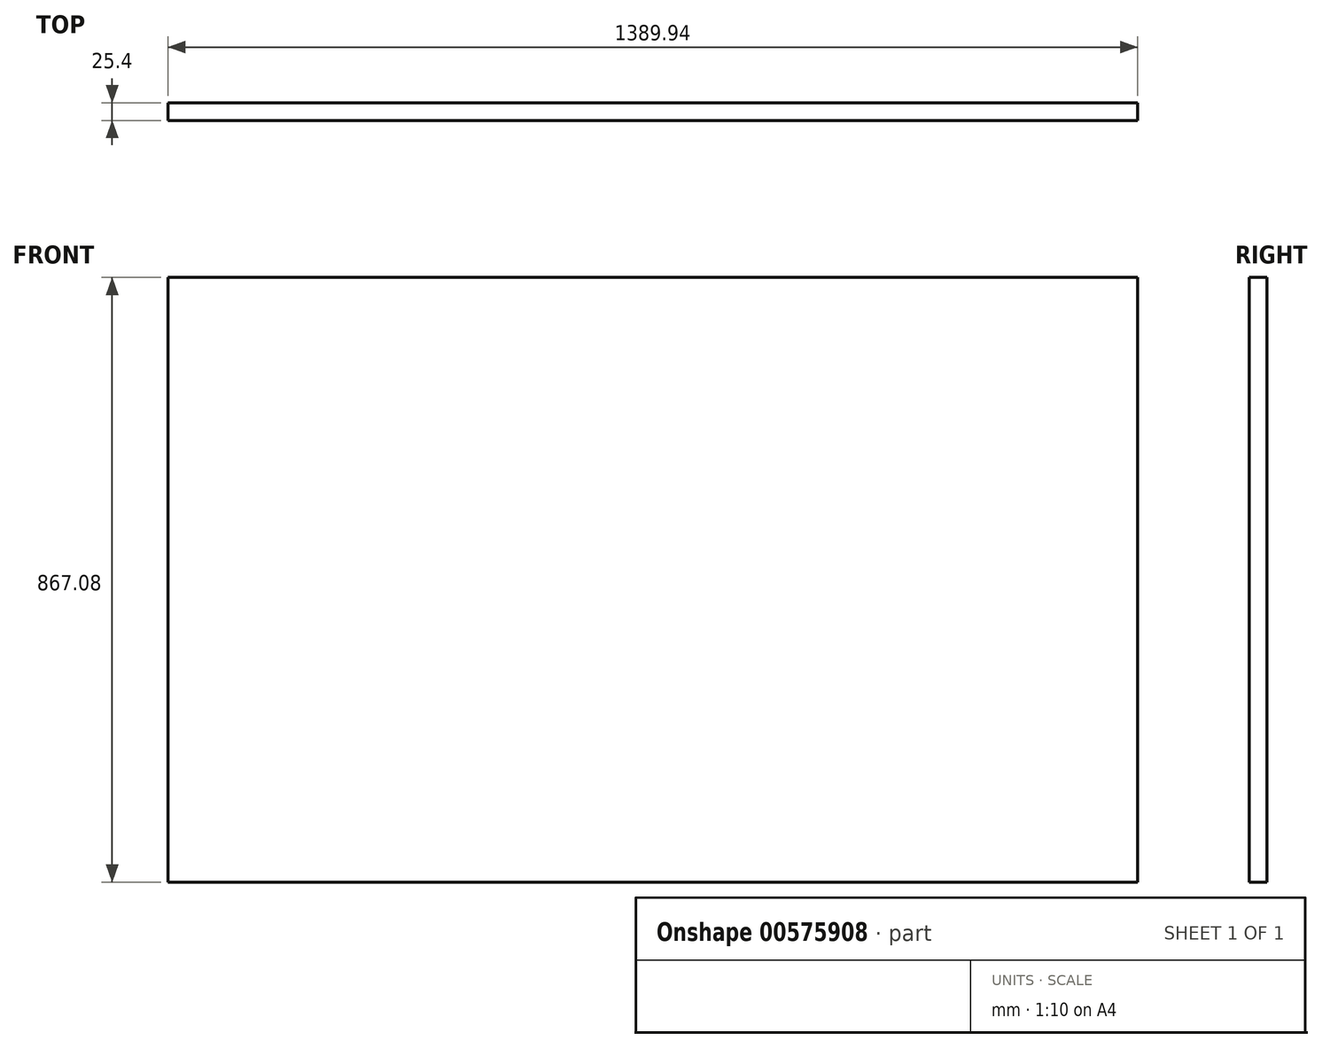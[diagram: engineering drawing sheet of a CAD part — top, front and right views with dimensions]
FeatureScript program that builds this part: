
annotation { "Feature Type Name" : "Feature", "Feature Type Description" : "" }
export const myFeature = defineFeature(function(context is Context, id is Id, definition is map)
    precondition{}
    {
        {
            var Q0;
            Q0=qCreatedBy(makeId("Front.planeOp"),FACE);
            var sketch = newSketch(context, id + "F0", { "sketchPlane" : qUnion([Q0])});
            skLineSegment(sketch, "E0.bottom", {"start": v(-1312.47, 180.4) * mm, "end": v(77.47, 180.4) * mm});
            skLineSegment(sketch, "E0.top", {"start": v(-1312.47, -686.7) * mm, "end": v(77.47, -686.7) * mm});
            skLineSegment(sketch, "E0.left", {"start": v(-1312.47, 180.4) * mm, "end": v(-1312.47, -686.7) * mm});
            skLineSegment(sketch, "E0.right", {"start": v(77.47, 180.4) * mm, "end": v(77.47, -686.7) * mm});
            skSolve(sketch);
        }
        {
            var Q0;
            Q0 = qSketchRegion(id + "F0", true);
            extrude(context, id + "F1", {"entities" : qUnion([Q0]), "depth" : 25.4 * mm, "offsetDistance" : 25.4 * mm});
        }
    });
